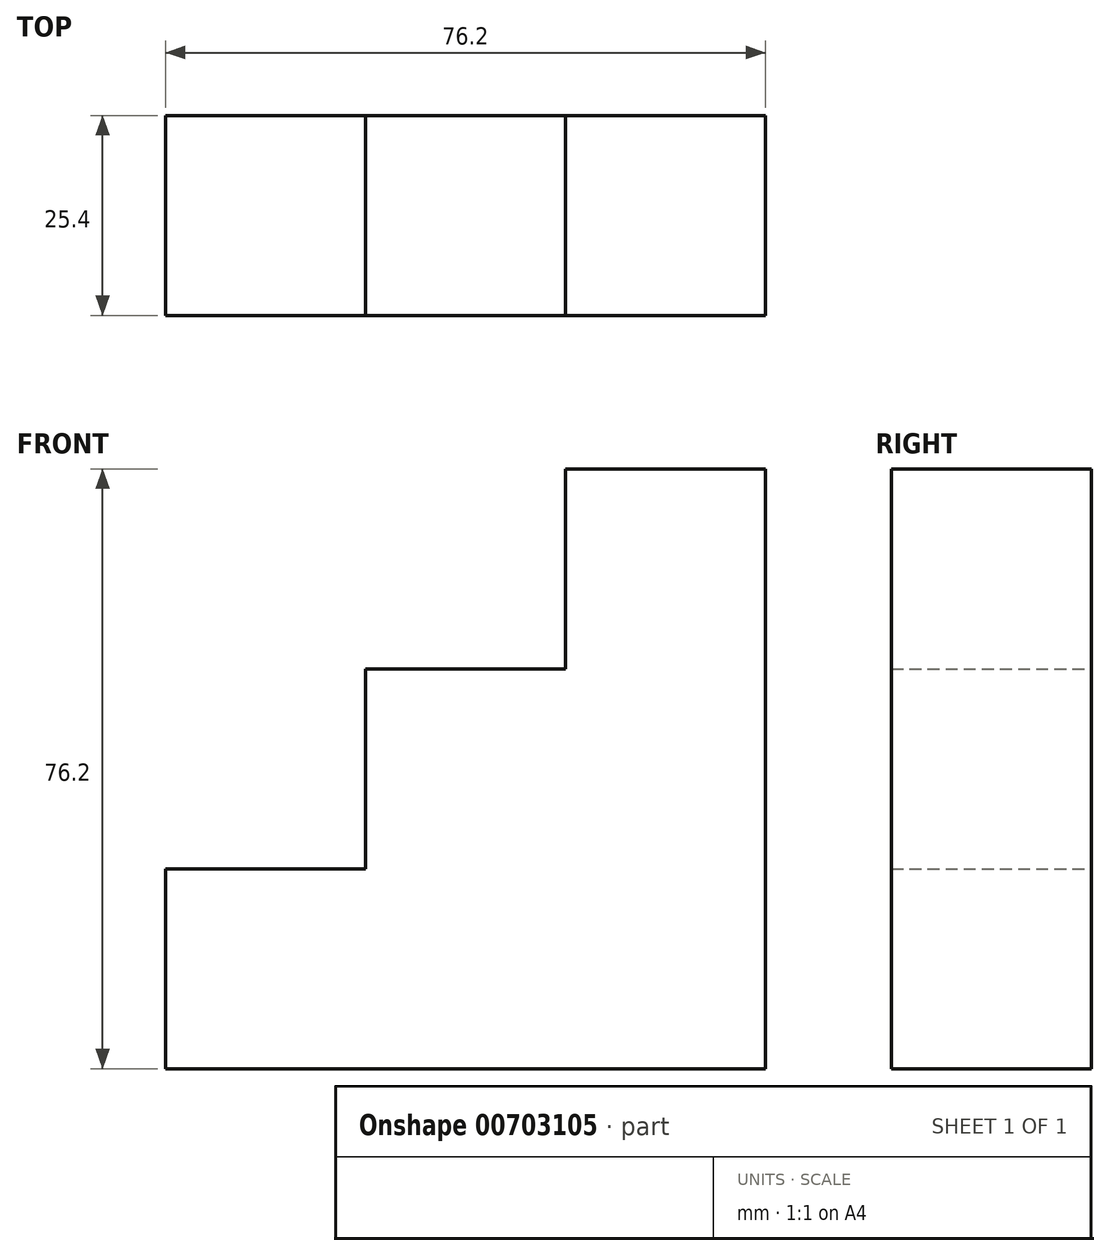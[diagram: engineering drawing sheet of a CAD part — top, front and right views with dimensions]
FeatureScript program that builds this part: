
annotation { "Feature Type Name" : "Feature", "Feature Type Description" : "" }
export const myFeature = defineFeature(function(context is Context, id is Id, definition is map)
    precondition{}
    {
        {
            var Q0;
            Q0=qCreatedBy(makeId("Front.planeOp"),FACE);
            var sketch = newSketch(context, id + "F0", { "sketchPlane" : qUnion([Q0])});
            skLineSegment(sketch, "E0", {"start": v(56.63, 53.19) * mm, "end": v(56.63, -23.01) * mm});
            skLineSegment(sketch, "E1", {"start": v(56.63, 53.19) * mm, "end": v(31.23, 53.19) * mm});
            skLineSegment(sketch, "E2", {"start": v(31.23, 53.19) * mm, "end": v(31.23, 27.79) * mm});
            skLineSegment(sketch, "E3", {"start": v(31.23, 27.79) * mm, "end": v(5.83, 27.79) * mm});
            skLineSegment(sketch, "E4", {"start": v(5.83, 27.79) * mm, "end": v(5.83, 2.39) * mm});
            skLineSegment(sketch, "E5", {"start": v(5.83, 2.39) * mm, "end": v(-19.57, 2.39) * mm});
            skLineSegment(sketch, "E6", {"start": v(-19.57, 2.39) * mm, "end": v(-19.57, -23.01) * mm});
            skLineSegment(sketch, "E7", {"start": v(-19.57, -23.01) * mm, "end": v(56.63, -23.01) * mm});
            skSolve(sketch);
        }
        {
            var Q0;
            Q0=makeQuery(id+"F0.imprint","IMPRINT",FACE,{"disambiguationData":[TD([[makeQuery(id+"F0.imprint","IMPRINT",EDGE,{"derivedFrom":sQuery(id+"F0.wireOp",EDGE,"E0")}),-1.0]])]});
            extrude(context, id + "F1", {"entities" : qUnion([Q0]), "depth" : 25.4 * mm, "offsetDistance" : 25.4 * mm});
        }
    });
